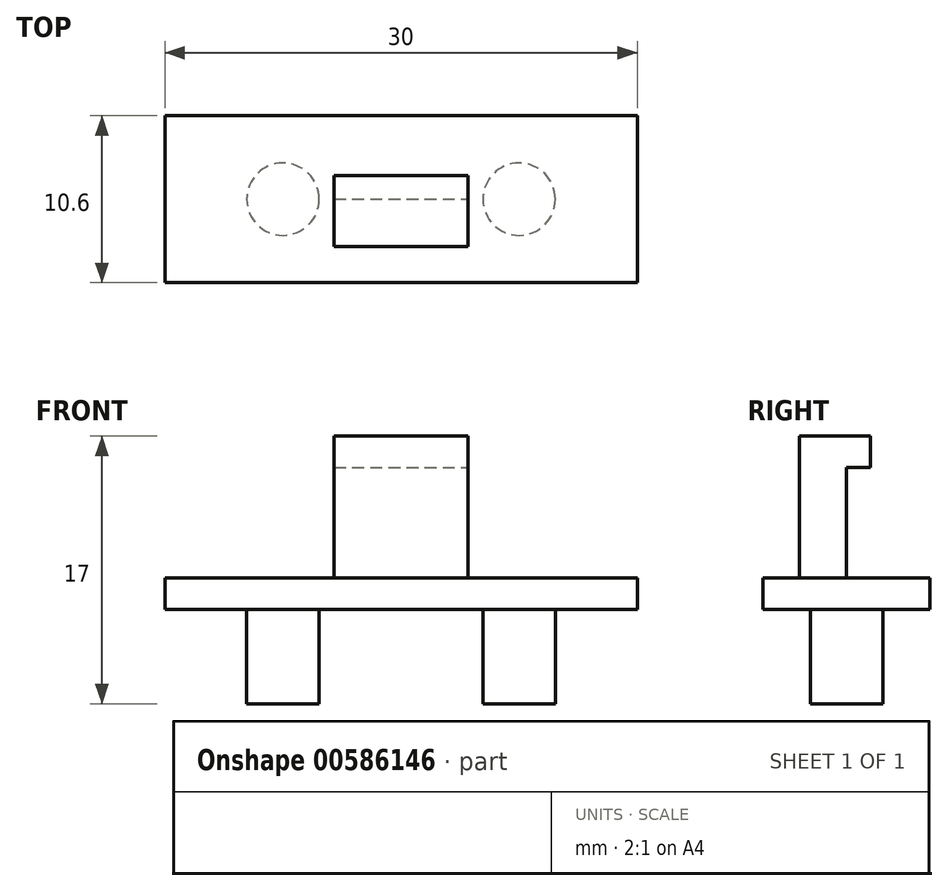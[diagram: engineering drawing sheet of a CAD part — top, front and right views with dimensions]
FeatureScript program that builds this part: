
annotation { "Feature Type Name" : "Feature", "Feature Type Description" : "" }
export const myFeature = defineFeature(function(context is Context, id is Id, definition is map)
    precondition{}
    {
        {
            var Q0;
            Q0=qCreatedBy(makeId("Top.planeOp"),FACE);
            var sketch = newSketch(context, id + "F0", { "sketchPlane" : qUnion([Q0])});
            skCircle(sketch, "E0", {"center": v(-7.5, 0) * mm, "radius": 2.3 * mm});
            skLineSegment(sketch, "E1.bottom", {"start": v(-15, 5.3) * mm, "end": v(0, 5.3) * mm});
            skLineSegment(sketch, "E1.top", {"start": v(-15, -5.3) * mm, "end": v(0, -5.3) * mm});
            skLineSegment(sketch, "E1.left", {"start": v(-15, 5.3) * mm, "end": v(-15, -5.3) * mm});
            skLineSegment(sketch, "E1.right", {"start": v(0, 5.3) * mm, "end": v(0, -5.3) * mm});
            skLineSegment(sketch, "E2.direction1", {"start": v(-15, -5.3) * mm, "end": v(0, -5.3) * mm, "construction": true});
            skLineSegment(sketch, "E3.0.1.0", {"start": v(15, 5.3) * mm, "end": v(15, -5.3) * mm});
            skLineSegment(sketch, "E3.6.1.0", {"start": v(0, 5.3) * mm, "end": v(15, 5.3) * mm});
            skLineSegment(sketch, "E3.9.1.0", {"start": v(0, -5.3) * mm, "end": v(15, -5.3) * mm});
            skCircle(sketch, "E3.12.1.0", {"center": v(7.5, 0) * mm, "radius": 2.3 * mm});
            skSolve(sketch);
        }
        {
            var Q0;
            Q0=makeQuery(id+"F0.imprint","IMPRINT",FACE,{"disambiguationData":[TD([[makeQuery(id+"F0.imprint","IMPRINT",EDGE,{"derivedFrom":sQuery(id+"F0.wireOp",EDGE,"E0")}),-1.0]])]});
            var Q1;
            Q1=makeQuery(id+"F0.imprint","IMPRINT",FACE,{"disambiguationData":[TD([[makeQuery(id+"F0.imprint","IMPRINT",EDGE,{"derivedFrom":sQuery(id+"F0.wireOp",EDGE,"E2.1.0.1")}),1.0]])]});
            var Q2;
            Q2=makeQuery(id+"F0.imprint","IMPRINT",FACE,{"disambiguationData":[TD([[makeQuery(id+"F0.imprint","IMPRINT",EDGE,{"derivedFrom":sQuery(id+"F0.wireOp",EDGE,"E2.2.0.1")}),1.0]])]});
            var Q3;
            Q3=makeQuery(id+"F0.imprint","IMPRINT",FACE,{"disambiguationData":[TD([[makeQuery(id+"F0.imprint","IMPRINT",EDGE,{"derivedFrom":sQuery(id+"F0.wireOp",EDGE,"E2.3.0.1")}),1.0]])]});
            var Q4;
            Q4=makeQuery(id+"F0.imprint","IMPRINT",FACE,{"disambiguationData":[TD([[makeQuery(id+"F0.imprint","IMPRINT",EDGE,{"derivedFrom":sQuery(id+"F0.wireOp",EDGE,"cdc6a2be-ecee-4a68-925e-44659f448387.0.4.0")}),-1.0]])]});
            var Q5;
            Q5=makeQuery(id+"F0.imprint","IMPRINT",FACE,{"disambiguationData":[TD([[makeQuery(id+"F0.imprint","IMPRINT",EDGE,{"derivedFrom":sQuery(id+"F0.wireOp",EDGE,"E3.0.1.0")}),-1.0]])]});
            extrude(context, id + "F1", {"entities" : qUnion([Q0, Q1, Q2, Q3, Q4, Q5]), "oppositeDirection" : true, "depth" : 2 * mm, "offsetDistance" : 25 * mm});
        }
        {
            var Q0;
            Q0=makeQuery(id+"F0.imprint","IMPRINT",FACE,{"disambiguationData":[TD([[makeQuery(id+"F0.imprint","IMPRINT",EDGE,{"derivedFrom":sQuery(id+"F0.wireOp",EDGE,"HJVtsFcj-nnXf-v6pU-8xeC-anOBP0SdkL5j")}),1.0]])]});
            var Q1;
            Q1=makeQuery(id+"F0.imprint","IMPRINT",FACE,{"disambiguationData":[TD([[makeQuery(id+"F0.imprint","IMPRINT",EDGE,{"derivedFrom":sQuery(id+"F0.wireOp",EDGE,"E2.1.0.4")}),1.0]])]});
            var Q2;
            Q2=makeQuery(id+"F0.imprint","IMPRINT",FACE,{"disambiguationData":[TD([[makeQuery(id+"F0.imprint","IMPRINT",EDGE,{"derivedFrom":sQuery(id+"F0.wireOp",EDGE,"E0")}),1.0]])]});
            var Q3;
            Q3=makeQuery(id+"F0.imprint","IMPRINT",FACE,{"disambiguationData":[TD([[makeQuery(id+"F0.imprint","IMPRINT",EDGE,{"derivedFrom":sQuery(id+"F0.wireOp",EDGE,"E2.2.0.4")}),1.0]])]});
            var Q4;
            Q4=makeQuery(id+"F0.imprint","IMPRINT",FACE,{"disambiguationData":[TD([[makeQuery(id+"F0.imprint","IMPRINT",EDGE,{"derivedFrom":sQuery(id+"F0.wireOp",EDGE,"E2.3.0.4")}),1.0]])]});
            var Q5;
            Q5=makeQuery(id+"F0.imprint","IMPRINT",FACE,{"disambiguationData":[TD([[makeQuery(id+"F0.imprint","IMPRINT",EDGE,{"derivedFrom":sQuery(id+"F0.wireOp",EDGE,"cdc6a2be-ecee-4a68-925e-44659f448387.12.4.0")}),1.0]])]});
            var Q6;
            Q6=makeQuery(id+"F0.imprint","IMPRINT",FACE,{"disambiguationData":[TD([[makeQuery(id+"F0.imprint","IMPRINT",EDGE,{"derivedFrom":sQuery(id+"F0.wireOp",EDGE,"E3.12.1.0")}),1.0]])]});
            extrude(context, id + "F2", {"entities" : qUnion([Q0, Q1, Q2, Q3, Q4, Q5, Q6]), "operationType" : NewBodyOperationType.ADD, "oppositeDirection" : true, "depth" : 8 * mm, "offsetDistance" : 25 * mm});
        }
        {
            var Q0;
            Q0=qCreatedBy(makeId("Top.planeOp"),FACE);
            var sketch = newSketch(context, id + "F3", { "sketchPlane" : qUnion([Q0])});
            skLineSegment(sketch, "E4.bottom", {"start": v(-4.25, 0) * mm, "end": v(4.25, 0) * mm});
            skLineSegment(sketch, "E4.top", {"start": v(-4.25, -3) * mm, "end": v(4.25, -3) * mm});
            skLineSegment(sketch, "E4.left", {"start": v(-4.25, 0) * mm, "end": v(-4.25, -3) * mm});
            skLineSegment(sketch, "E4.right", {"start": v(4.25, 0) * mm, "end": v(4.25, -3) * mm});
            skLineSegment(sketch, "E5.bottom", {"start": v(-4.25, 1.5) * mm, "end": v(4.25, 1.5) * mm});
            skLineSegment(sketch, "E5.left", {"start": v(-4.25, 1.5) * mm, "end": v(-4.25, 0) * mm});
            skLineSegment(sketch, "E5.right", {"start": v(4.25, 1.5) * mm, "end": v(4.25, 0) * mm});
            skSolve(sketch);
        }
        {
            var Q0;
            Q0=makeQuery(id+"F3.imprint","IMPRINT",FACE,{"disambiguationData":[TD([[makeQuery(id+"F3.imprint","IMPRINT",EDGE,{"derivedFrom":sQuery(id+"F3.wireOp",EDGE,"E4.top")}),1.0]])]});
            extrude(context, id + "F4", {"entities" : qUnion([Q0]), "operationType" : NewBodyOperationType.ADD, "depth" : 9 * mm, "offsetDistance" : 25 * mm});
        }
        {
            var Q0;
            Q0=makeQuery(id+"F3.imprint","IMPRINT",FACE,{"disambiguationData":[TD([[makeQuery(id+"F3.imprint","IMPRINT",EDGE,{"derivedFrom":sQuery(id+"F3.wireOp",EDGE,"E5.bottom")}),-1.0]])]});
            extrude(context, id + "F5", {"entities" : qUnion([Q0]), "operationType" : NewBodyOperationType.ADD, "depth" : 9 * mm, "offsetDistance" : 25 * mm, "hasSecondDirection" : true, "secondDirectionOppositeDirection" : false, "secondDirectionDepth" : 7 * mm});
        }
    });
